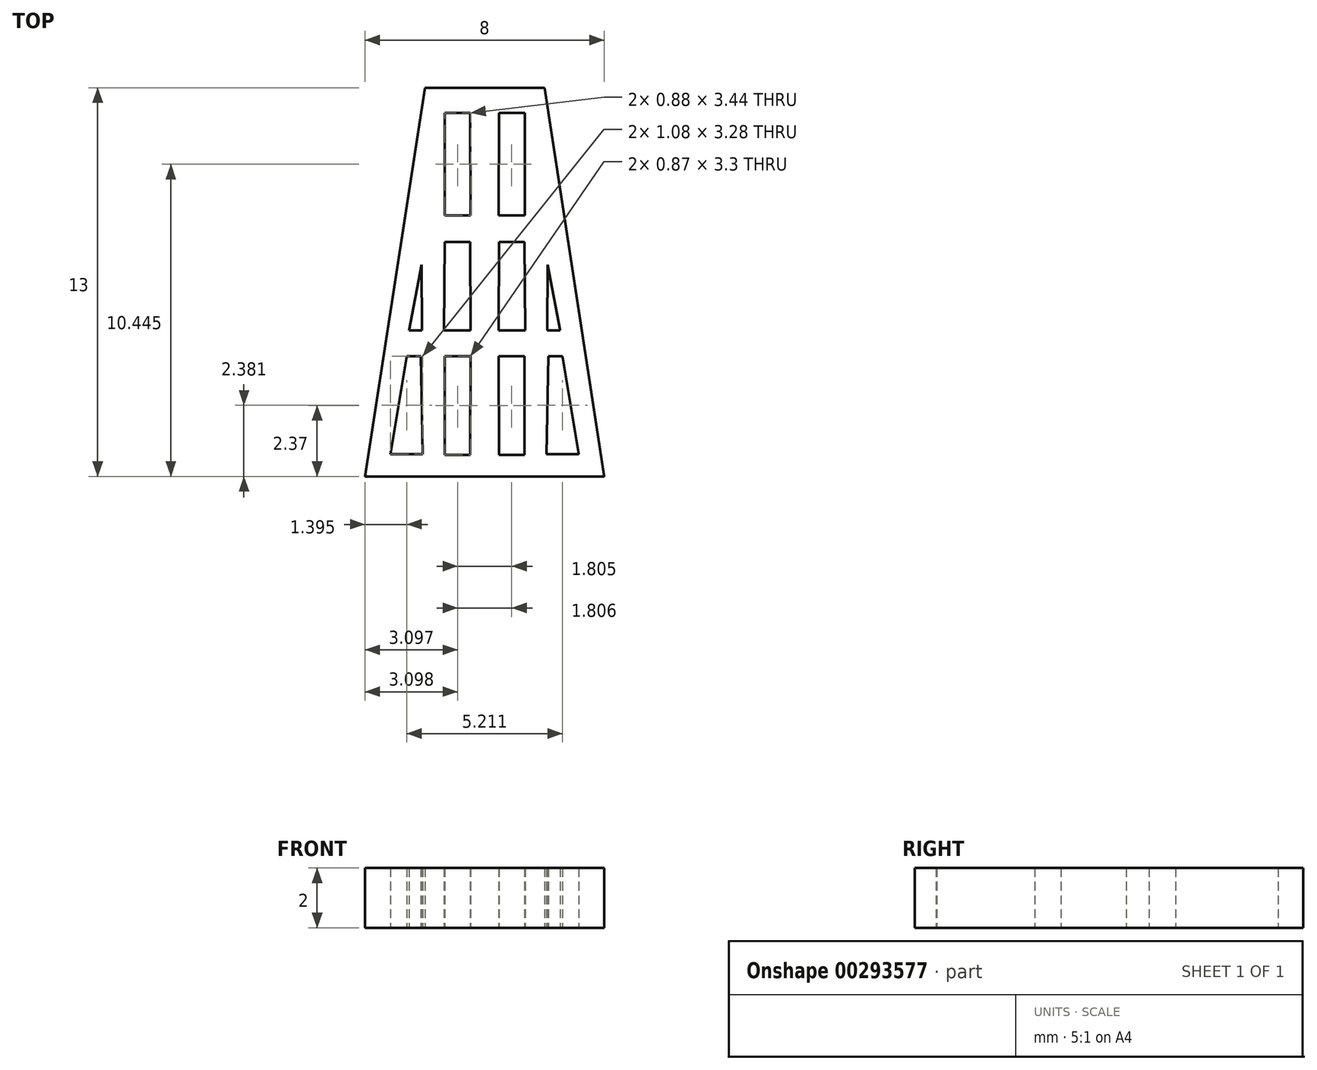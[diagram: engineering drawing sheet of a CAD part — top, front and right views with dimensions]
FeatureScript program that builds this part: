
annotation { "Feature Type Name" : "Feature", "Feature Type Description" : "" }
export const myFeature = defineFeature(function(context is Context, id is Id, definition is map)
    precondition{}
    {
        {
            var Q0;
            Q0=qCreatedBy(makeId("Top.planeOp"),FACE);
            var sketch = newSketch(context, id + "F0", { "sketchPlane" : qUnion([Q0])});
            skLineSegment(sketch, "E0", {"start": v(0, 6.48) * mm, "end": v(-2, 6.48) * mm});
            skLineSegment(sketch, "E1", {"start": v(-2, 6.48) * mm, "end": v(-4, -6.52) * mm});
            skLineSegment(sketch, "E2", {"start": v(-4, -6.52) * mm, "end": v(0, -6.52) * mm});
            skLineSegment(sketch, "E3", {"start": v(-0.48, 5.64) * mm, "end": v(-1.34, 5.64) * mm});
            skLineSegment(sketch, "E4", {"start": v(-1.34, 5.64) * mm, "end": v(-1.34, 2.2) * mm});
            skLineSegment(sketch, "E5", {"start": v(-1.34, 2.2) * mm, "end": v(-0.46, 2.2) * mm});
            skLineSegment(sketch, "E6", {"start": v(-0.46, 2.2) * mm, "end": v(-0.48, 5.64) * mm});
            skLineSegment(sketch, "E7", {"start": v(-1.34, 1.33) * mm, "end": v(-0.48, 1.33) * mm});
            skLineSegment(sketch, "E8", {"start": v(-0.48, 1.33) * mm, "end": v(-0.47, -1.63) * mm});
            skLineSegment(sketch, "E9", {"start": v(-0.47, -1.63) * mm, "end": v(-1.35, -1.63) * mm});
            skLineSegment(sketch, "E10", {"start": v(-1.35, -1.63) * mm, "end": v(-1.34, 1.33) * mm});
            skLineSegment(sketch, "E11", {"start": v(-1.34, -2.5) * mm, "end": v(-0.47, -2.5) * mm});
            skLineSegment(sketch, "E12", {"start": v(-0.47, -2.5) * mm, "end": v(-0.48, -5.8) * mm});
            skLineSegment(sketch, "E13", {"start": v(-0.48, -5.8) * mm, "end": v(-1.34, -5.8) * mm});
            skLineSegment(sketch, "E14", {"start": v(-1.34, -5.8) * mm, "end": v(-1.34, -2.5) * mm});
            skLineSegment(sketch, "E15", {"start": v(-2.13, -2.5) * mm, "end": v(-2.6, -2.5) * mm});
            skLineSegment(sketch, "E16", {"start": v(-2.6, -2.5) * mm, "end": v(-3.15, -5.78) * mm});
            skLineSegment(sketch, "E17", {"start": v(-3.15, -5.78) * mm, "end": v(-2.06, -5.77) * mm});
            skLineSegment(sketch, "E18", {"start": v(-2.06, -5.77) * mm, "end": v(-2.13, -2.5) * mm});
            skLineSegment(sketch, "E19", {"start": v(-2.1, 0.56) * mm, "end": v(-2.1, -1.63) * mm});
            skLineSegment(sketch, "E20", {"start": v(-2.1, -1.63) * mm, "end": v(-2.52, -1.63) * mm});
            skLineSegment(sketch, "E21", {"start": v(-2.52, -1.63) * mm, "end": v(-2.1, 0.56) * mm});
            skLineSegment(sketch, "E22.MirrorCS", {"start": v(0, 6.48) * mm, "end": v(2, 6.48) * mm});
            skLineSegment(sketch, "E23.MirrorCS", {"start": v(2, 6.48) * mm, "end": v(4, -6.52) * mm});
            skLineSegment(sketch, "E24.MirrorCS", {"start": v(4, -6.52) * mm, "end": v(0, -6.52) * mm});
            skLineSegment(sketch, "E25.MirrorCS", {"start": v(0.48, -5.8) * mm, "end": v(1.34, -5.8) * mm});
            skLineSegment(sketch, "E26.MirrorCS", {"start": v(3.15, -5.78) * mm, "end": v(2.06, -5.77) * mm});
            skLineSegment(sketch, "E27.MirrorCS", {"start": v(2.6, -2.5) * mm, "end": v(3.15, -5.78) * mm});
            skLineSegment(sketch, "E28.MirrorCS", {"start": v(2.06, -5.77) * mm, "end": v(2.13, -2.5) * mm});
            skLineSegment(sketch, "E29.MirrorCS", {"start": v(1.34, -5.8) * mm, "end": v(1.34, -2.5) * mm});
            skLineSegment(sketch, "E30.MirrorCS", {"start": v(0.47, -2.5) * mm, "end": v(0.48, -5.8) * mm});
            skLineSegment(sketch, "E31.MirrorCS", {"start": v(1.34, -2.5) * mm, "end": v(0.47, -2.5) * mm});
            skLineSegment(sketch, "E32.MirrorCS", {"start": v(2.13, -2.5) * mm, "end": v(2.6, -2.5) * mm});
            skLineSegment(sketch, "E33.MirrorCS", {"start": v(0.47, -1.63) * mm, "end": v(1.35, -1.63) * mm});
            skLineSegment(sketch, "E34.MirrorCS", {"start": v(1.35, -1.63) * mm, "end": v(1.34, 1.33) * mm});
            skLineSegment(sketch, "E35.MirrorCS", {"start": v(0.48, 1.33) * mm, "end": v(0.47, -1.63) * mm});
            skLineSegment(sketch, "E36.MirrorCS", {"start": v(1.34, 1.33) * mm, "end": v(0.48, 1.33) * mm});
            skLineSegment(sketch, "E37.MirrorCS", {"start": v(1.34, 2.2) * mm, "end": v(0.46, 2.2) * mm});
            skLineSegment(sketch, "E38.MirrorCS", {"start": v(1.34, 5.64) * mm, "end": v(1.34, 2.2) * mm});
            skLineSegment(sketch, "E39.MirrorCS", {"start": v(0.46, 2.2) * mm, "end": v(0.48, 5.64) * mm});
            skLineSegment(sketch, "E40.MirrorCS", {"start": v(2.1, -1.63) * mm, "end": v(2.52, -1.63) * mm});
            skLineSegment(sketch, "E41.MirrorCS", {"start": v(2.1, 0.56) * mm, "end": v(2.1, -1.63) * mm});
            skLineSegment(sketch, "E42.MirrorCS", {"start": v(2.52, -1.63) * mm, "end": v(2.1, 0.56) * mm});
            skLineSegment(sketch, "E43.MirrorCS", {"start": v(0.48, 5.64) * mm, "end": v(1.34, 5.64) * mm});
            skSolve(sketch);
        }
        {
            var Q0;
            Q0=makeQuery(id+"F0.imprint","IMPRINT",FACE,{"disambiguationData":[TD([[makeQuery(id+"F0.imprint","IMPRINT",EDGE,{"derivedFrom":sQuery(id+"F0.wireOp",EDGE,"E0")}),1.0]])]});
            extrude(context, id + "F1", {"entities" : qUnion([Q0]), "depth" : 2 * mm, "offsetDistance" : 25 * mm});
        }
    });
